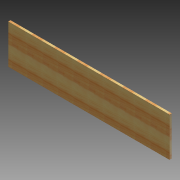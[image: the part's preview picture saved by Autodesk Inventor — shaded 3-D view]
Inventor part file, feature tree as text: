
AUTODESK INVENTOR PART (.ipt)
format: ipt  version: 2012 (Build 160160000, 160)  size: 80,384 bytes
history: native  units: in
note: dims shown in document units (in); Inventor stores cm internally (conversion verified against a paired STEP export)
features: extrude x1, sketch x1
ambient origin geometry x8: Origin, YZ Plane, XZ Plane, XY Plane, X Axis, Y Axis, Z Axis, Center Point
bodies: Solid1 (feature_tree)
feature tree (2):
  extrude  "Extrusion1"  Depth=9.0in
  sketch  "Sketch1"  dims[d0=37.0in d1=9.0in d2=0.5in d3=0.0in]
